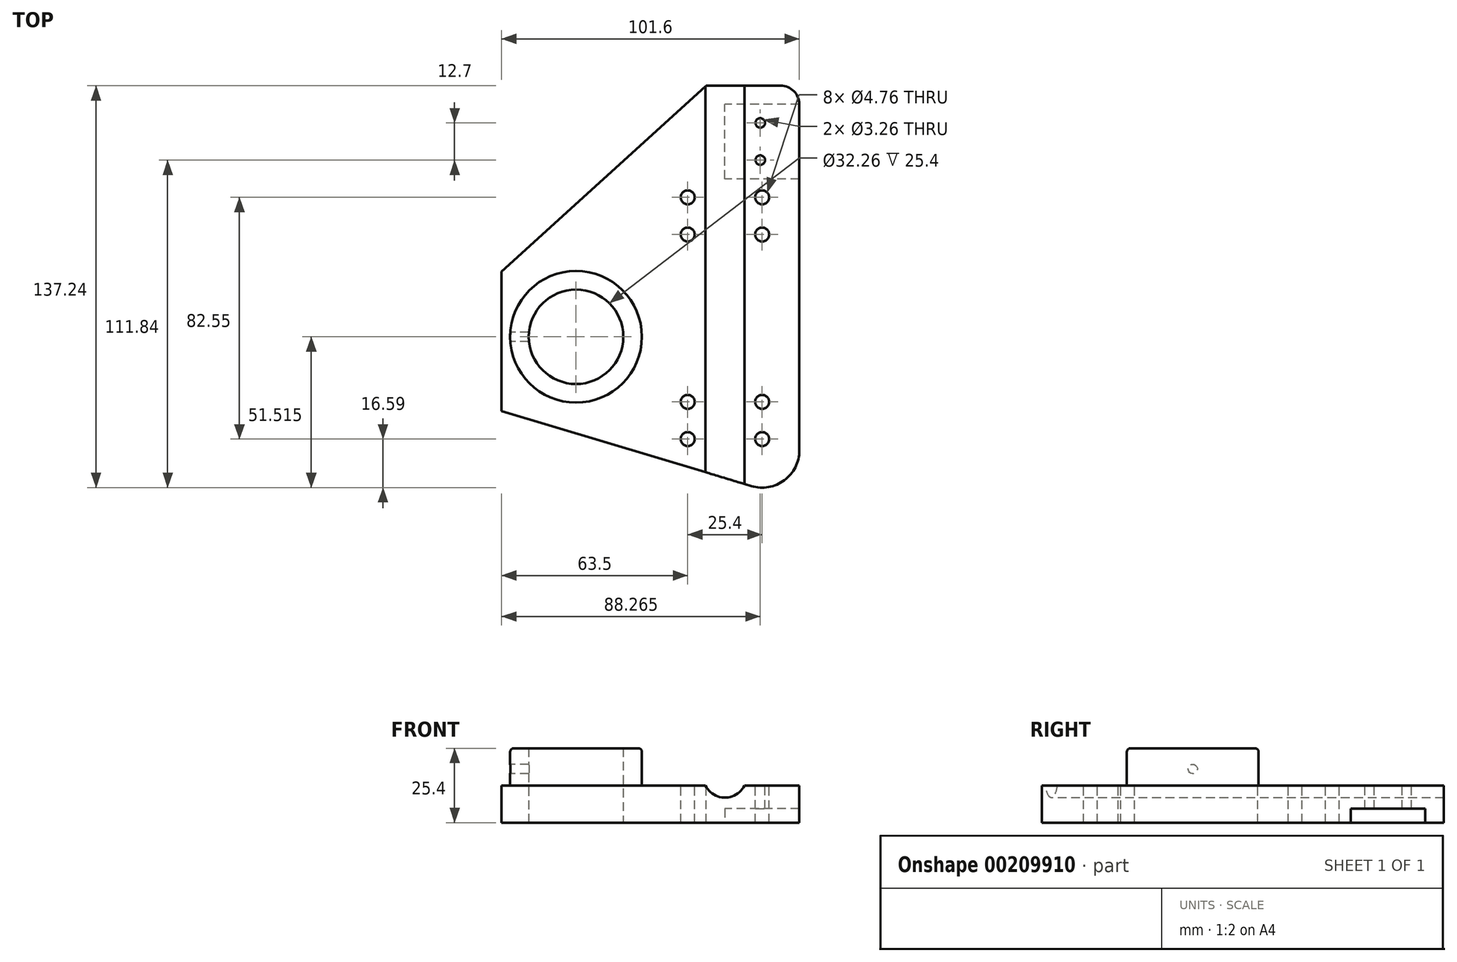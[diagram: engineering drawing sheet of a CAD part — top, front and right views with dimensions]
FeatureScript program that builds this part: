
annotation { "Feature Type Name" : "Feature", "Feature Type Description" : "" }
export const myFeature = defineFeature(function(context is Context, id is Id, definition is map)
    precondition{}
    {
        {
            var Q0;
            Q0=qCreatedBy(makeId("Top.planeOp"),FACE);
            var sketch = newSketch(context, id + "F0", { "sketchPlane" : qUnion([Q0])});
            skLineSegment(sketch, "E0.bottom", {"start": v(0, 0) * mm, "end": v(95.25, 0) * mm});
            skLineSegment(sketch, "E0.top", {"start": v(6.35, 139.7) * mm, "end": v(95.25, 139.7) * mm});
            skLineSegment(sketch, "E0.left", {"start": v(0, 0) * mm, "end": v(0, 133.35) * mm});
            skLineSegment(sketch, "E0.right", {"start": v(101.6, 6.35) * mm, "end": v(101.6, 133.35) * mm});
            skPoint(sketch, "E1.visualSharp", {"position": v(0, 139.7) * mm});
            skPoint(sketch, "E2.visualSharp", {"position": v(101.6, 139.7) * mm});
            skArc(sketch, "E2.filletArc", {"start": v(101.6, 133.35) * mm, "mid": v(99.74, 137.84) * mm, "end": v(95.25, 139.7) * mm});
            skPoint(sketch, "E3.visualSharp", {"position": v(101.6, 0) * mm});
            skArc(sketch, "E3.filletArc", {"start": v(95.25, 0) * mm, "mid": v(99.74, 1.86) * mm, "end": v(101.6, 6.35) * mm});
            skCircle(sketch, "E4", {"center": v(25.4, 53.98) * mm, "radius": 16.13 * mm});
            skArc(sketch, "E5.filletArc", {"start": v(6.35, 139.7) * mm, "mid": v(1.86, 137.84) * mm, "end": v(0, 133.35) * mm});
            skSolve(sketch);
        }
        {
            var Q0;
            Q0 = qSketchRegion(id + "F0", true);
            extrude(context, id + "F1", {"entities" : qUnion([Q0]), "depth" : 12.7 * mm});
        }
        {
            var Q0;
            Q0=makeQuery(id+"F1.opExtrude","CAP_FACE",FACE,{"disambiguationData":[OSD([sQuery(id+"F0.wireOp",EDGE,"E0.bottom"),sQuery(id+"F0.wireOp",EDGE,"E0.top"),sQuery(id+"F0.wireOp",EDGE,"E0.right"),sQuery(id+"F0.wireOp",EDGE,"5klZIDEJ-8arz-1rak-FGRC-5Zb9QQEC7unF"),sQuery(id+"F0.wireOp",EDGE,"E1.filletArc"),sQuery(id+"F0.wireOp",EDGE,"E2.filletArc"),sQuery(id+"F0.wireOp",EDGE,"E3.filletArc"),sQuery(id+"F0.wireOp",EDGE,"E4")])],"isStart":false});
            var sketch = newSketch(context, id + "F2", { "sketchPlane" : qUnion([Q0])});
            skCircle(sketch, "E6", {"center": v(25.4, 53.98) * mm, "radius": 16.13 * mm});
            skCircle(sketch, "E7.0", {"center": v(25.4, 53.98) * mm, "radius": 22.48 * mm});
            skSolve(sketch);
        }
        {
            var Q0;
            Q0 = qSketchRegion(id + "F2", true);
            extrude(context, id + "F3", {"entities" : qUnion([Q0]), "operationType" : NewBodyOperationType.ADD, "depth" : 12.7 * mm});
        }
        {
            var Q0;
            Q0=makeQuery(id+"F1.opExtrude","CAP_FACE",FACE,{"disambiguationData":[OSD([sQuery(id+"F0.wireOp",EDGE,"E0.bottom"),sQuery(id+"F0.wireOp",EDGE,"E0.top"),sQuery(id+"F0.wireOp",EDGE,"E0.right"),sQuery(id+"F0.wireOp",EDGE,"5klZIDEJ-8arz-1rak-FGRC-5Zb9QQEC7unF"),sQuery(id+"F0.wireOp",EDGE,"E1.filletArc"),sQuery(id+"F0.wireOp",EDGE,"E2.filletArc"),sQuery(id+"F0.wireOp",EDGE,"E3.filletArc"),sQuery(id+"F0.wireOp",EDGE,"E4")])],"isStart":false});
            var sketch = newSketch(context, id + "F4", { "sketchPlane" : qUnion([Q0])});
            skLineSegment(sketch, "E8", {"start": v(88.27, 0) * mm, "end": v(88.27, 139.7) * mm, "construction": true});
            skPoint(sketch, "E9", {"position": v(88.27, 127) * mm});
            skPoint(sketch, "E10", {"position": v(88.27, 114.3) * mm});
            skSolve(sketch);
        }
        {
            var Q0;
            Q0=sQuery(id+"F4.wireOp",VERTEX,"E9");
            var Q1;
            Q1=sQuery(id+"F4.wireOp",VERTEX,"E10");
            var Q2;
            Q2=makeQuery(id+"F1.opExtrude","SWEPT_BODY",BODY,{"disambiguationData":[OSD([sQuery(id+"F0.wireOp",EDGE,"E0.bottom"),sQuery(id+"F0.wireOp",EDGE,"E0.top"),sQuery(id+"F0.wireOp",EDGE,"E0.left"),sQuery(id+"F0.wireOp",EDGE,"E0.right"),sQuery(id+"F0.wireOp",EDGE,"E2.filletArc"),sQuery(id+"F0.wireOp",EDGE,"E3.filletArc"),sQuery(id+"F0.wireOp",EDGE,"E4"),sQuery(id+"F0.wireOp",EDGE,"E5.filletArc")])]});
            hole(context, id + "F5", {"style" : HoleStyle.SIMPLE, "endStyle" : HoleEndStyle.BLIND, "standardTappedOrClearance" : lookupTablePath({ "standard" : "ANSI", "fit" : "Normal (ASME)", "size" : "#4", "type" : "Clearance" }), "standardBlindInLast" : lookupTablePath({ "fit" : "Free", "standard" : "ANSI", "size" : "#4", "type" : "Clearance" }), "holeDiameter" : 3.26 * mm, "holeDepth" : 19.05 * mm, "startFromSketch" : true, "locations" : qUnion([Q0, Q1]), "scope" : qUnion([Q2])});
        }
        {
            var Q0;
            Q0=makeQuery(id+"F1.opExtrude","CAP_FACE",FACE,{"disambiguationData":[OSD([sQuery(id+"F0.wireOp",EDGE,"E0.bottom"),sQuery(id+"F0.wireOp",EDGE,"E0.top"),sQuery(id+"F0.wireOp",EDGE,"E0.left"),sQuery(id+"F0.wireOp",EDGE,"E0.right"),sQuery(id+"F0.wireOp",EDGE,"E2.filletArc"),sQuery(id+"F0.wireOp",EDGE,"E3.filletArc"),sQuery(id+"F0.wireOp",EDGE,"E4"),sQuery(id+"F0.wireOp",EDGE,"E5.filletArc")])],"isStart":false});
            var sketch = newSketch(context, id + "F6", { "sketchPlane" : qUnion([Q0])});
            skLineSegment(sketch, "E11", {"start": v(0, 28.58) * mm, "end": v(95.25, 0) * mm});
            skLineSegment(sketch, "E12", {"start": v(95.25, 0) * mm, "end": v(0, 0) * mm});
            skLineSegment(sketch, "E13", {"start": v(0, 0) * mm, "end": v(0, 28.57) * mm});
            skLineSegment(sketch, "E14", {"start": v(0, 76.2) * mm, "end": v(69.85, 139.7) * mm});
            skLineSegment(sketch, "E15", {"start": v(69.85, 139.7) * mm, "end": v(0, 139.7) * mm});
            skLineSegment(sketch, "E16", {"start": v(0, 139.7) * mm, "end": v(0, 76.2) * mm});
            skSolve(sketch);
        }
        {
            var Q0;
            Q0 = qSketchRegion(id + "F6", true);
            extrude(context, id + "F7", {"entities" : qUnion([Q0]), "operationType" : NewBodyOperationType.REMOVE, "endBound" : BoundingType.UP_TO_NEXT, "oppositeDirection" : true, "depth" : 25.4 * mm});
        }
        {
            var Q0;
            Q0=makeQuery(id+"F7.boolean.opBoolean","COPY",EDGE,{"derivedFrom":makeQuery(id+"F7.opExtrude","SWEPT_EDGE",EDGE,{"disambiguationData":[OSD([sQuery(id+"F0.wireOp",EDGE,"E0.left"),sQuery(id+"F6.wireOp",EDGE,"E11"),sQuery(id+"F6.wireOp",EDGE,"E13")])]})});
            var Q1;
            Q1=makeQuery(id+"F7.boolean.opBoolean","COPY",EDGE,{"derivedFrom":makeQuery(id+"F7.opExtrude","SWEPT_EDGE",EDGE,{"disambiguationData":[OSD([sQuery(id+"F0.wireOp",EDGE,"E0.left"),sQuery(id+"F6.wireOp",EDGE,"E14"),sQuery(id+"F6.wireOp",EDGE,"E16")])]})});
            var Q2;
            Q2=makeQuery(id+"F7.boolean.opBoolean","COPY",EDGE,{"derivedFrom":makeQuery(id+"F7.opExtrude","SWEPT_EDGE",EDGE,{"disambiguationData":[OSD([sQuery(id+"F0.wireOp",EDGE,"E0.top"),sQuery(id+"F6.wireOp",EDGE,"E14"),sQuery(id+"F6.wireOp",EDGE,"E15")])]})});
            var Q3;
            {var subQ0=sQuery(id+"F0.wireOp",EDGE,"E3.filletArc");var subQ1=sQuery(id+"F0.wireOp",EDGE,"E0.bottom");Q3=makeQuery(id+"F7.boolean.opBoolean","MERGE",EDGE,{"derivedFrom":[makeQuery(id+"F1.opExtrude","SWEPT_EDGE",EDGE,{"disambiguationData":[OSD([subQ1,subQ0])]}),makeQuery(id+"F7.opExtrude","SWEPT_EDGE",EDGE,{"disambiguationData":[OSD([subQ1,subQ0,sQuery(id+"F6.wireOp",EDGE,"E11"),sQuery(id+"F6.wireOp",EDGE,"E12")])]})]});}
            fillet(context, id + "F8", {"entities" : qUnion([Q0, Q1, Q2, Q3]), "radius" : 12.7 * mm, "tangentPropagation" : true, "allowEdgeOverflow" : false});
        }
        {
            var Q0;
            Q0=qCreatedBy(makeId("Front.planeOp"),FACE);
            var sketch = newSketch(context, id + "F9", { "sketchPlane" : qUnion([Q0])});
            skCircle(sketch, "E17", {"center": v(76.2, 15.88) * mm, "radius": 7.37 * mm});
            skSolve(sketch);
        }
        {
            var Q0;
            Q0=makeQuery(id+"F9.imprint","IMPRINT",FACE,{"disambiguationData":[TD([[makeQuery(id+"F9.imprint","IMPRINT",EDGE,{"derivedFrom":sQuery(id+"F9.wireOp",EDGE,"E17")}),1.0]])]});
            extrude(context, id + "F10", {"entities" : qUnion([Q0]), "operationType" : NewBodyOperationType.REMOVE, "oppositeDirection" : true, "depth" : 152.4 * mm});
        }
        {
            var Q0;
            Q0=makeQuery(id+"F3.opExtrude","CAP_EDGE",EDGE,{"disambiguationData":[OSD([sQuery(id+"F2.wireOp",EDGE,"E7.0")])],"isStart":false});
            fillet(context, id + "F11", {"entities" : qUnion([Q0]), "radius" : 1.27 * mm, "tangentPropagation" : true, "allowEdgeOverflow" : false});
        }
        {
            var Q0;
            Q0=qCreatedBy(makeId("Right.planeOp"),FACE);
            var sketch = newSketch(context, id + "F12", { "sketchPlane" : qUnion([Q0])});
            skLineSegment(sketch, "E18", {"start": v(31.5, 12.7) * mm, "end": v(31.5, 23.98) * mm});
            skLineSegment(sketch, "E19", {"start": v(76.45, 23.98) * mm, "end": v(76.45, 12.7) * mm});
            skLineSegment(sketch, "E20.0", {"start": v(15.16, 12.7) * mm, "end": v(133.35, 12.7) * mm});
            skLineSegment(sketch, "E21", {"start": v(31.5, 18.34) * mm, "end": v(76.45, 18.34) * mm, "construction": true});
            skPoint(sketch, "E22", {"position": v(53.98, 18.34) * mm});
            skSolve(sketch);
        }
        {
            var Q0;
            Q0=sQuery(id+"F12.wireOp",VERTEX,"E22");
            var Q1;
            Q1=makeQuery(id+"F1.opExtrude","SWEPT_BODY",BODY,{"disambiguationData":[OSD([sQuery(id+"F0.wireOp",EDGE,"E0.bottom"),sQuery(id+"F0.wireOp",EDGE,"E0.top"),sQuery(id+"F0.wireOp",EDGE,"E0.left"),sQuery(id+"F0.wireOp",EDGE,"E0.right"),sQuery(id+"F0.wireOp",EDGE,"E2.filletArc"),sQuery(id+"F0.wireOp",EDGE,"E3.filletArc"),sQuery(id+"F0.wireOp",EDGE,"E4"),sQuery(id+"F0.wireOp",EDGE,"E5.filletArc")])]});
            hole(context, id + "F13", {"style" : HoleStyle.SIMPLE, "endStyle" : HoleEndStyle.BLIND, "oppositeDirection" : true, "holeDiameter" : 3.17 * mm, "holeDepth" : 12.7 * mm, "startFromSketch" : true, "locations" : qUnion([Q0]), "scope" : qUnion([Q1])});
        }
        {
            var Q0;
            {var subQ0=sQuery(id+"F0.wireOp",EDGE,"E2.filletArc");var subQ1=sQuery(id+"F0.wireOp",EDGE,"E0.right");var subQ2=sQuery(id+"F0.wireOp",EDGE,"E0.top");var subQ4=sQuery(id+"F0.wireOp",EDGE,"E3.filletArc");var subQ5=sQuery(id+"F0.wireOp",EDGE,"E0.bottom");Q0=makeQuery(id+"F10.boolean.opBoolean","SPLIT",FACE,{"disambiguationData":[TD([makeQuery(id+"F1.opExtrude","SWEPT_FACE",FACE,{"disambiguationData":[OSD([subQ2])]})])],"derivedFrom":makeQuery(id+"F1.opExtrude","CAP_FACE",FACE,{"disambiguationData":[OSD([subQ5,subQ2,sQuery(id+"F0.wireOp",EDGE,"E0.left"),subQ1,subQ0,subQ4,sQuery(id+"F0.wireOp",EDGE,"E4"),sQuery(id+"F0.wireOp",EDGE,"E5.filletArc")])],"isStart":false})});}
            var sketch = newSketch(context, id + "F14", { "sketchPlane" : qUnion([Q0])});
            skLineSegment(sketch, "E23.bottom", {"start": v(88.9, 101.6) * mm, "end": v(63.5, 101.6) * mm});
            skLineSegment(sketch, "E23.top", {"start": v(88.9, 88.9) * mm, "end": v(63.5, 88.9) * mm});
            skLineSegment(sketch, "E23.left", {"start": v(88.9, 101.6) * mm, "end": v(88.9, 88.9) * mm});
            skLineSegment(sketch, "E23.right", {"start": v(63.5, 101.6) * mm, "end": v(63.5, 88.9) * mm});
            skLineSegment(sketch, "E24.bottom", {"start": v(88.9, 31.75) * mm, "end": v(63.5, 31.75) * mm});
            skLineSegment(sketch, "E24.top", {"start": v(88.9, 19.05) * mm, "end": v(63.5, 19.05) * mm});
            skLineSegment(sketch, "E24.left", {"start": v(88.9, 31.75) * mm, "end": v(88.9, 19.05) * mm});
            skLineSegment(sketch, "E24.right", {"start": v(63.5, 31.75) * mm, "end": v(63.5, 19.05) * mm});
            skSolve(sketch);
        }
        {
            var Q0;
            Q0=sQuery(id+"F14.wireOp",VERTEX,"E23.bottom.start");
            var Q1;
            Q1=sQuery(id+"F14.wireOp",VERTEX,"E23.left.end");
            var Q2;
            Q2=sQuery(id+"F14.wireOp",VERTEX,"E23.right.start");
            var Q3;
            Q3=sQuery(id+"F14.wireOp",VERTEX,"E23.right.end");
            var Q4;
            Q4=sQuery(id+"F14.wireOp",VERTEX,"E24.right.start");
            var Q5;
            Q5=sQuery(id+"F14.wireOp",VERTEX,"E24.top.end");
            var Q6;
            Q6=sQuery(id+"F14.wireOp",VERTEX,"E24.left.end");
            var Q7;
            Q7=sQuery(id+"F14.wireOp",VERTEX,"E24.left.start");
            var Q8;
            Q8=makeQuery(id+"F1.opExtrude","SWEPT_BODY",BODY,{"disambiguationData":[OSD([sQuery(id+"F0.wireOp",EDGE,"E0.bottom"),sQuery(id+"F0.wireOp",EDGE,"E0.top"),sQuery(id+"F0.wireOp",EDGE,"E0.left"),sQuery(id+"F0.wireOp",EDGE,"E0.right"),sQuery(id+"F0.wireOp",EDGE,"E2.filletArc"),sQuery(id+"F0.wireOp",EDGE,"E3.filletArc"),sQuery(id+"F0.wireOp",EDGE,"E4"),sQuery(id+"F0.wireOp",EDGE,"E5.filletArc")])]});
            hole(context, id + "F15", {"style" : HoleStyle.SIMPLE, "endStyle" : HoleEndStyle.BLIND, "holeDiameter" : 4.76 * mm, "holeDepth" : 19.05 * mm, "startFromSketch" : true, "locations" : qUnion([Q0, Q1, Q2, Q3, Q4, Q5, Q6, Q7]), "scope" : qUnion([Q8])});
        }
        {
            var Q0;
            Q0=makeQuery(id+"F1.opExtrude","CAP_FACE",FACE,{"disambiguationData":[OSD([sQuery(id+"F0.wireOp",EDGE,"E0.bottom"),sQuery(id+"F0.wireOp",EDGE,"E0.top"),sQuery(id+"F0.wireOp",EDGE,"E0.left"),sQuery(id+"F0.wireOp",EDGE,"E0.right"),sQuery(id+"F0.wireOp",EDGE,"E2.filletArc"),sQuery(id+"F0.wireOp",EDGE,"E3.filletArc"),sQuery(id+"F0.wireOp",EDGE,"E4"),sQuery(id+"F0.wireOp",EDGE,"E5.filletArc")])],"isStart":true});
            var sketch = newSketch(context, id + "F16", { "sketchPlane" : qUnion([Q0])});
            skLineSegment(sketch, "E25.bottom", {"start": v(101.6, -107.85) * mm, "end": v(76.2, -107.85) * mm});
            skLineSegment(sketch, "E25.top", {"start": v(101.6, -133.35) * mm, "end": v(76.2, -133.35) * mm});
            skLineSegment(sketch, "E25.left", {"start": v(101.6, -107.85) * mm, "end": v(101.6, -133.35) * mm});
            skLineSegment(sketch, "E25.right", {"start": v(76.2, -107.85) * mm, "end": v(76.2, -133.35) * mm});
            skSolve(sketch);
        }
        {
            var Q0;
            Q0 = qSketchRegion(id + "F16", true);
            extrude(context, id + "F17", {"entities" : qUnion([Q0]), "operationType" : NewBodyOperationType.REMOVE, "oppositeDirection" : true, "depth" : 4.76 * mm});
        }
    });
